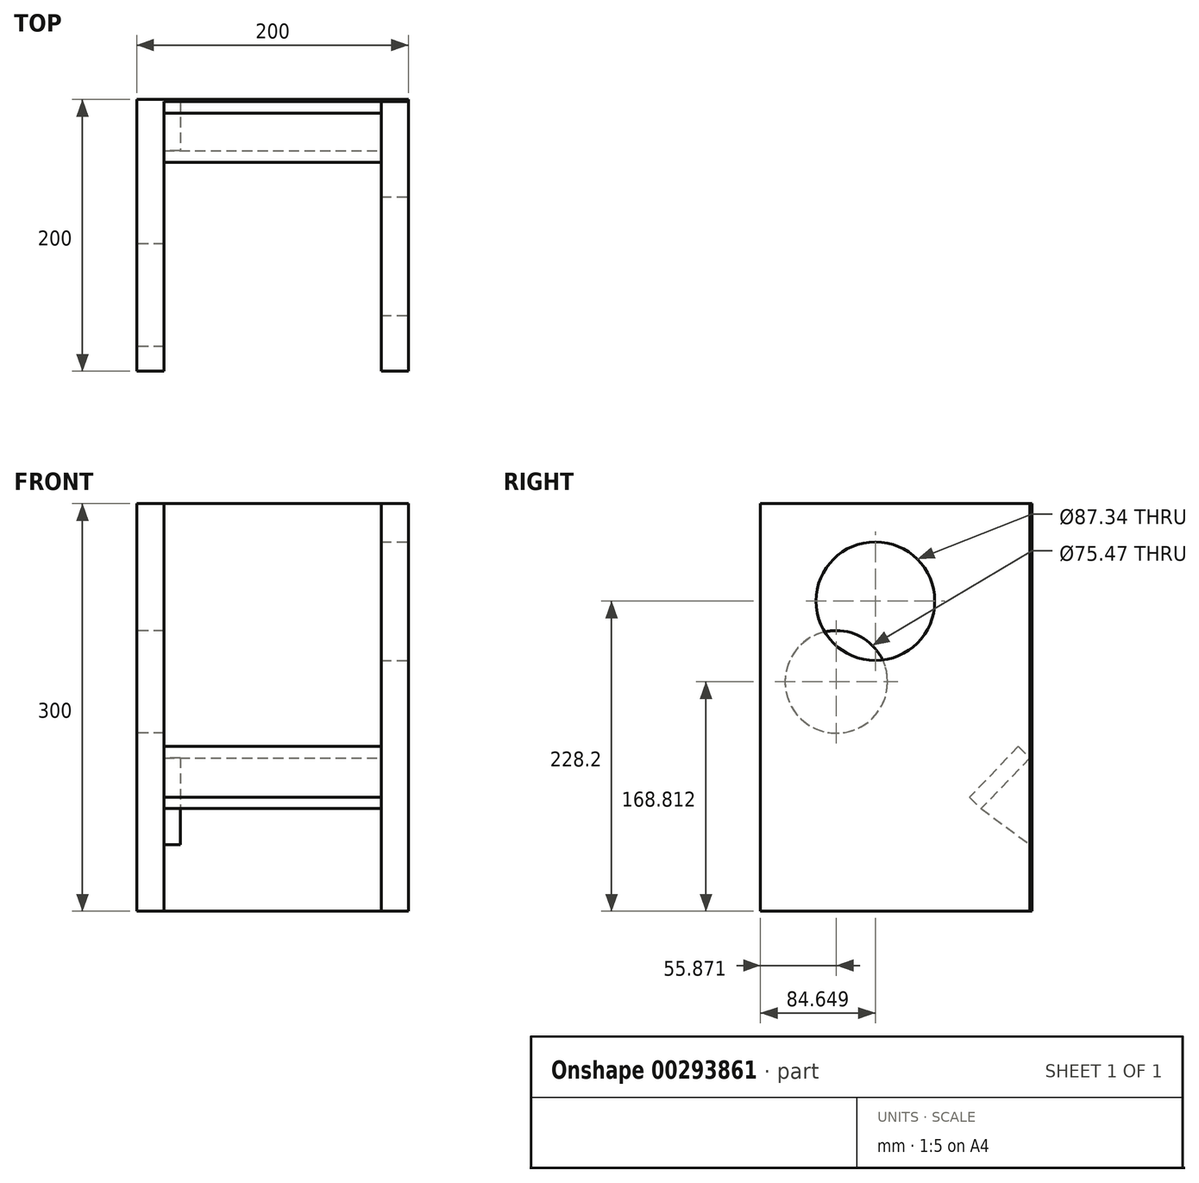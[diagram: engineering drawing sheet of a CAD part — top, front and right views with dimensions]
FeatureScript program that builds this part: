
annotation { "Feature Type Name" : "Feature", "Feature Type Description" : "" }
export const myFeature = defineFeature(function(context is Context, id is Id, definition is map)
    precondition{}
    {
        {
            var Q0;
            Q0=qCreatedBy(makeId("Front.planeOp"),FACE);
            var sketch = newSketch(context, id + "F0", { "sketchPlane" : qUnion([Q0])});
            skLineSegment(sketch, "E0.bottom", {"start": v(0, 0) * mm, "end": v(200, 0) * mm});
            skLineSegment(sketch, "E0.top", {"start": v(0, 300) * mm, "end": v(200, 300) * mm});
            skLineSegment(sketch, "E0.left", {"start": v(0, 0) * mm, "end": v(0, 300) * mm});
            skLineSegment(sketch, "E0.right", {"start": v(200, 0) * mm, "end": v(200, 300) * mm});
            skSolve(sketch);
        }
        {
            var Q0;
            Q0=makeQuery(id+"F0.imprint","IMPRINT",FACE,{"disambiguationData":[TD([[makeQuery(id+"F0.imprint","IMPRINT",EDGE,{"derivedFrom":sQuery(id+"F0.wireOp",EDGE,"E0.bottom")}),1.0]])]});
            extrude(context, id + "F1", {"entities" : qUnion([Q0]), "depth" : 1.5 * mm});
        }
        {
            var Q0;
            Q0=qCreatedBy(makeId("Front.planeOp"),FACE);
            var sketch = newSketch(context, id + "F2", { "sketchPlane" : qUnion([Q0])});
            skLineSegment(sketch, "E1.bottom", {"start": v(0, 0) * mm, "end": v(20, 0) * mm});
            skLineSegment(sketch, "E1.top", {"start": v(0, 300) * mm, "end": v(20, 300) * mm});
            skLineSegment(sketch, "E1.left", {"start": v(0, 0) * mm, "end": v(0, 300) * mm});
            skLineSegment(sketch, "E1.right", {"start": v(20, 0) * mm, "end": v(20, 300) * mm});
            skSolve(sketch);
        }
        {
            var Q0;
            Q0 = qSketchRegion(id + "F2", true);
            extrude(context, id + "F3", {"entities" : qUnion([Q0]), "operationType" : NewBodyOperationType.ADD, "depth" : 200 * mm});
        }
        {
            var Q0;
            Q0=makeQuery(id+"F3.opExtrude","SWEPT_FACE",FACE,{"disambiguationData":[OSD([sQuery(id+"F2.wireOp",EDGE,"E1.right")])]});
            var sketch = newSketch(context, id + "F4", { "sketchPlane" : qUnion([Q0])});
            skLineSegment(sketch, "E2", {"start": v(-37.57, 75.47) * mm, "end": v(-1.5, 49.07) * mm});
            skLineSegment(sketch, "E3", {"start": v(-1.5, 49.07) * mm, "end": v(-1.5, 112.87) * mm});
            skLineSegment(sketch, "E4", {"start": v(-1.5, 112.87) * mm, "end": v(-37.57, 75.47) * mm});
            skSolve(sketch);
        }
        {
            var Q0;
            Q0=makeQuery(id+"F4.imprint","IMPRINT",FACE,{"disambiguationData":[TD([[makeQuery(id+"F4.imprint","IMPRINT",EDGE,{"derivedFrom":sQuery(id+"F4.wireOp",EDGE,"E2")}),1.0]])]});
            extrude(context, id + "F5", {"entities" : qUnion([Q0]), "operationType" : NewBodyOperationType.ADD, "depth" : 12 * mm});
        }
        {
            var Q0;
            Q0=makeQuery(id+"F5.opExtrude","SWEPT_FACE",FACE,{"disambiguationData":[OSD([sQuery(id+"F4.wireOp",EDGE,"E4")])]});
            var sketch = newSketch(context, id + "F6", { "sketchPlane" : qUnion([Q0])});
            skLineSegment(sketch, "E5.bottom", {"start": v(20, 80.2) * mm, "end": v(180, 80.2) * mm});
            skLineSegment(sketch, "E5.top", {"start": v(20, 28.24) * mm, "end": v(180, 28.24) * mm});
            skLineSegment(sketch, "E5.left", {"start": v(20, 80.2) * mm, "end": v(20, 28.24) * mm});
            skLineSegment(sketch, "E5.right", {"start": v(180, 80.2) * mm, "end": v(180, 28.24) * mm});
            skSolve(sketch);
        }
        {
            var Q0;
            Q0 = qSketchRegion(id + "F6", true);
            extrude(context, id + "F7", {"entities" : qUnion([Q0]), "depth" : 12 * mm});
        }
        {
            var Q0;
            Q0=qCreatedBy(makeId("Front.planeOp"),FACE);
            var sketch = newSketch(context, id + "F8", { "sketchPlane" : qUnion([Q0])});
            skLineSegment(sketch, "E6.bottom", {"start": v(200, 0) * mm, "end": v(180, 0) * mm});
            skLineSegment(sketch, "E6.top", {"start": v(200, 300) * mm, "end": v(180, 300) * mm});
            skLineSegment(sketch, "E6.left", {"start": v(200, 0) * mm, "end": v(200, 300) * mm});
            skLineSegment(sketch, "E6.right", {"start": v(180, 0) * mm, "end": v(180, 300) * mm});
            skSolve(sketch);
        }
        {
            var Q0;
            Q0=makeQuery(id+"F8.imprint","IMPRINT",FACE,{"disambiguationData":[TD([[makeQuery(id+"F8.imprint","IMPRINT",EDGE,{"derivedFrom":sQuery(id+"F8.wireOp",EDGE,"E6.bottom")}),-1.0]])]});
            extrude(context, id + "F9", {"entities" : qUnion([Q0]), "depth" : 200 * mm});
        }
        {
            var Q0;
            Q0=makeQuery(id+"F9.opExtrude","SWEPT_FACE",FACE,{"disambiguationData":[OSD([sQuery(id+"F8.wireOp",EDGE,"E6.left")])]});
            var sketch = newSketch(context, id + "F10", { "sketchPlane" : qUnion([Q0])});
            skCircle(sketch, "E7", {"center": v(-115.35, 228.2) * mm, "radius": 43.67 * mm});
            skSolve(sketch);
        }
        {
            var Q0;
            Q0=makeQuery(id+"F10.imprint","IMPRINT",FACE,{"disambiguationData":[TD([[makeQuery(id+"F10.imprint","IMPRINT",EDGE,{"derivedFrom":sQuery(id+"F10.wireOp",EDGE,"E7")}),1.0]])]});
            var Q1;
            Q1=sQuery(id+"F10.wireOp",EDGE,"E7");
            extrude(context, id + "F11", {"entities" : qUnion([Q0]), "operationType" : NewBodyOperationType.REMOVE, "surfaceEntities" : qUnion([Q1]), "oppositeDirection" : true, "depth" : 30 * mm});
        }
        {
            var Q0;
            Q0=makeQuery(id+"F3.boolean.opBoolean","MERGE",FACE,{"derivedFrom":[makeQuery(id+"F1.opExtrude","SWEPT_FACE",FACE,{"disambiguationData":[OSD([sQuery(id+"F0.wireOp",EDGE,"E0.left")])]}),makeQuery(id+"F3.opExtrude","SWEPT_FACE",FACE,{"disambiguationData":[OSD([sQuery(id+"F2.wireOp",EDGE,"E1.left")])]})]});
            var sketch = newSketch(context, id + "F12", { "sketchPlane" : qUnion([Q0])});
            skCircle(sketch, "E8", {"center": v(144.13, 168.81) * mm, "radius": 37.73 * mm});
            skSolve(sketch);
        }
        {
            var Q0;
            Q0 = qSketchRegion(id + "F12", true);
            extrude(context, id + "F13", {"entities" : qUnion([Q0]), "operationType" : NewBodyOperationType.REMOVE, "oppositeDirection" : true, "depth" : 25 * mm});
        }
    });
